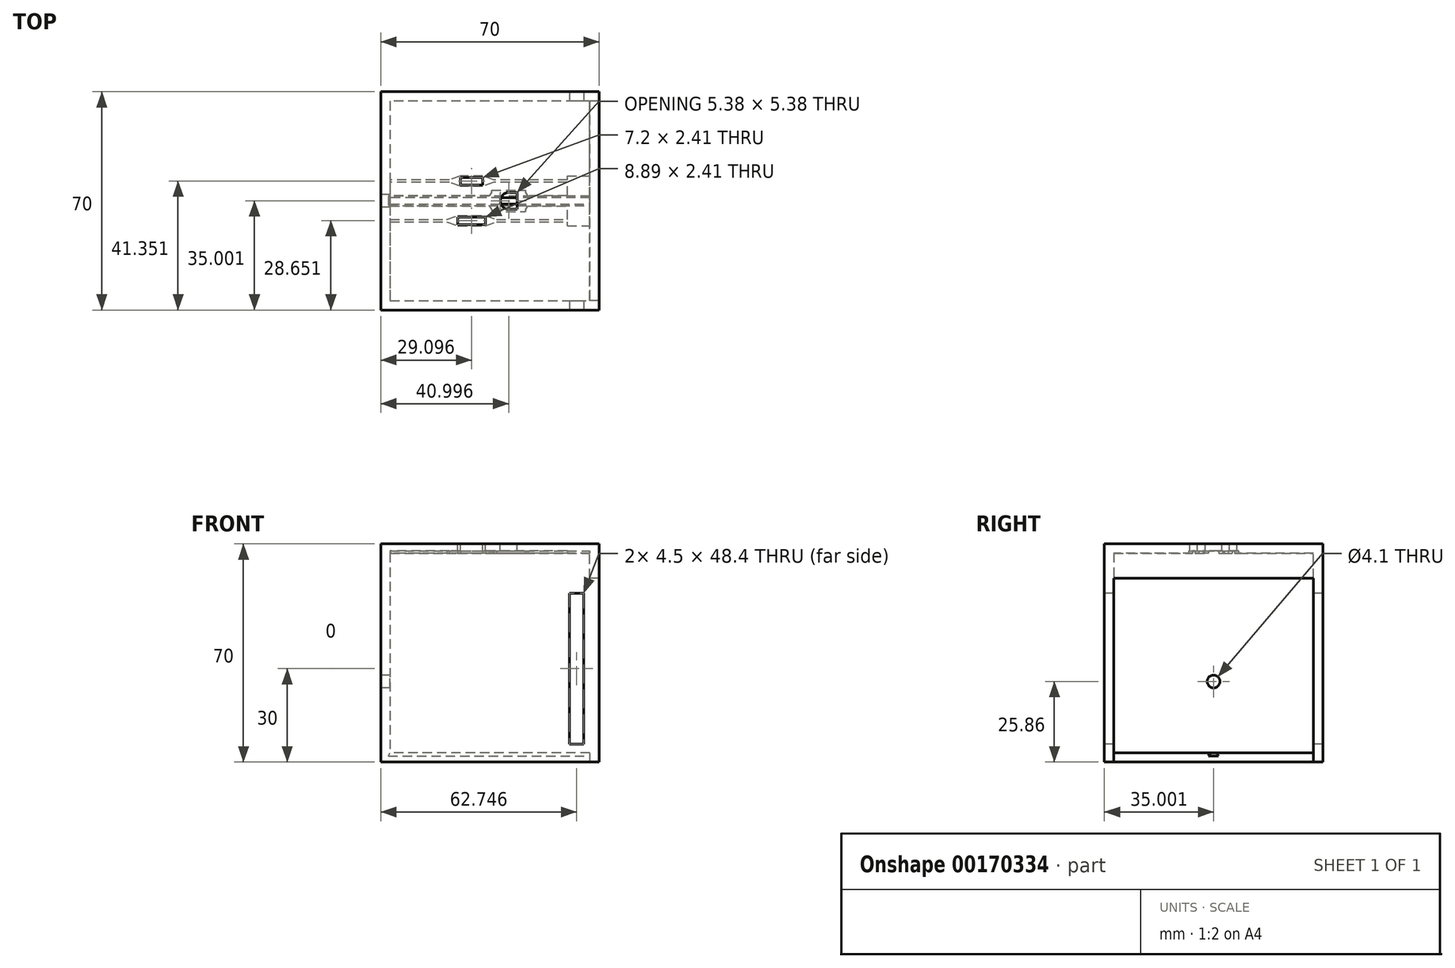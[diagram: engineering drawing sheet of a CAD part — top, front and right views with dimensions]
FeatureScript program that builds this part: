
annotation { "Feature Type Name" : "Feature", "Feature Type Description" : "" }
export const myFeature = defineFeature(function(context is Context, id is Id, definition is map)
    precondition{}
    {
        {
            var Q0;
            Q0=qCreatedBy(makeId("Top.planeOp"),FACE);
            var sketch = newSketch(context, id + "F0", { "sketchPlane" : qUnion([Q0])});
            skLineSegment(sketch, "E0", {"start": v(-33.77, 36.66) * mm, "end": v(-33.77, -33.34) * mm});
            skLineSegment(sketch, "E1", {"start": v(-33.77, -33.34) * mm, "end": v(36.23, -33.34) * mm});
            skLineSegment(sketch, "E2", {"start": v(36.23, -33.34) * mm, "end": v(36.23, 36.66) * mm});
            skLineSegment(sketch, "E3", {"start": v(36.23, 36.66) * mm, "end": v(-33.77, 36.66) * mm});
            skSolve(sketch);
        }
        {
            var Q0;
            Q0=makeQuery(id+"F0.imprint","IMPRINT",FACE,{"disambiguationData":[TD([[makeQuery(id+"F0.imprint","IMPRINT",EDGE,{"derivedFrom":sQuery(id+"F0.wireOp",EDGE,"E0")}),1.0]])]});
            extrude(context, id + "F1", {"entities" : qUnion([Q0]), "depth" : 70 * mm});
        }
        {
            var Q0;
            Q0=makeQuery(id+"F1.opExtrude","SWEPT_FACE",FACE,{"disambiguationData":[OSD([sQuery(id+"F0.wireOp",EDGE,"E2")])]});
            shell(context, id + "F2", {"entities" : qUnion([Q0]), "thickness" : 3 * mm});
        }
        {
            var Q0;
            Q0=makeQuery(id+"F1.opExtrude","CAP_FACE",FACE,{"disambiguationData":[OSD([sQuery(id+"F0.wireOp",EDGE,"E0"),sQuery(id+"F0.wireOp",EDGE,"E1"),sQuery(id+"F0.wireOp",EDGE,"E2"),sQuery(id+"F0.wireOp",EDGE,"E3")])],"isStart":false});
            var sketch = newSketch(context, id + "F3", { "sketchPlane" : qUnion([Q0])});
            skLineSegment(sketch, "E4.bottom", {"start": v(-9.12, -5.9) * mm, "end": v(-0.23, -5.9) * mm});
            skLineSegment(sketch, "E4.top", {"start": v(-9.12, -3.48) * mm, "end": v(-0.23, -3.48) * mm});
            skLineSegment(sketch, "E4.left", {"start": v(-9.12, -5.9) * mm, "end": v(-9.12, -3.48) * mm});
            skLineSegment(sketch, "E4.right", {"start": v(-0.23, -5.9) * mm, "end": v(-0.23, -3.48) * mm});
            skCircle(sketch, "E5", {"center": v(7.23, 1.66) * mm, "radius": 2.69 * mm});
            skLineSegment(sketch, "E6", {"start": v(7.23, -1.03) * mm, "end": v(9.92, -1.03) * mm});
            skLineSegment(sketch, "E7", {"start": v(9.92, -1.03) * mm, "end": v(9.92, 4.35) * mm});
            skLineSegment(sketch, "E8", {"start": v(9.92, 4.35) * mm, "end": v(7.23, 4.35) * mm});
            skLineSegment(sketch, "E9.bottom", {"start": v(-8.27, 6.8) * mm, "end": v(-1.07, 6.8) * mm});
            skLineSegment(sketch, "E9.top", {"start": v(-8.27, 9.22) * mm, "end": v(-1.07, 9.22) * mm});
            skLineSegment(sketch, "E9.left", {"start": v(-8.27, 6.8) * mm, "end": v(-8.27, 9.22) * mm});
            skLineSegment(sketch, "E9.right", {"start": v(-1.07, 6.8) * mm, "end": v(-1.07, 9.22) * mm});
            skSolve(sketch);
        }
        {
            var Q0;
            Q0=makeQuery(id+"F3.imprint","IMPRINT",FACE,{"disambiguationData":[TD([[makeQuery(id+"F3.imprint","IMPRINT",EDGE,{"derivedFrom":sQuery(id+"F3.wireOp",EDGE,"D6qbh7yJ-Ymuc-Tgfk-DwN8-qGhhH3okYrwW.bottom")}),-1.0]])]});
            var Q1;
            Q1=makeQuery(id+"F3.imprint","IMPRINT",FACE,{"disambiguationData":[TD([[makeQuery(id+"F3.imprint","IMPRINT",EDGE,{"derivedFrom":sQuery(id+"F3.wireOp",EDGE,"E4.bottom")}),1.0]])]});
            var Q2;
            {var subQ0=sQuery(id+"F3.wireOp",EDGE,"E5");var subQ1=makeQuery(id+"F3.imprint","INTERSECT",VERTEX,{"derivedFrom":[subQ0,sQuery(id+"F3.wireOp",EDGE,"E6")]});Q2=makeQuery(id+"F3.imprint","IMPRINT",FACE,{"disambiguationData":[TD([[makeQuery(id+"F3.imprint","IMPRINT",EDGE,{"disambiguationData":[TD([[subQ1,1.0]])],"derivedFrom":subQ0}),1.0]])]});}
            var Q3;
            {var subQ0=sQuery(id+"F3.wireOp",EDGE,"E6");Q3=makeQuery(id+"F3.imprint","IMPRINT",FACE,{"disambiguationData":[TD([[makeQuery(id+"F3.imprint","IMPRINT",EDGE,{"derivedFrom":subQ0}),1.0]])]});}
            var Q4;
            Q4=makeQuery(id+"F3.imprint","IMPRINT",FACE,{"disambiguationData":[TD([[makeQuery(id+"F3.imprint","IMPRINT",EDGE,{"derivedFrom":sQuery(id+"F3.wireOp",EDGE,"E9.bottom")}),1.0]])]});
            var Q5;
            {var subQ0=sQuery(id+"F3.wireOp",EDGE,"E8");Q5=makeQuery(id+"F3.imprint","IMPRINT",FACE,{"disambiguationData":[TD([[makeQuery(id+"F3.imprint","IMPRINT",EDGE,{"derivedFrom":subQ0}),1.0]])]});}
            extrude(context, id + "F4", {"entities" : qUnion([Q0, Q1, Q2, Q3, Q4, Q5]), "operationType" : NewBodyOperationType.REMOVE, "oppositeDirection" : true, "depth" : 2.54 * mm});
        }
        {
            var Q0;
            {var subQ0=sQuery(id+"F0.wireOp",EDGE,"E3");var subQ1=sQuery(id+"F0.wireOp",EDGE,"E2");var subQ2=sQuery(id+"F0.wireOp",EDGE,"E1");var subQ3=sQuery(id+"F0.wireOp",EDGE,"E0");Q0=makeQuery(id+"F2.opShell","OFFSET_FACE",FACE,{"disambiguationData":[OSD([subQ3,subQ2,subQ1,subQ0]),TDD([makeQuery(id+"F1.opExtrude","CAP_FACE",FACE,{"disambiguationData":[OSD([subQ3,subQ2,subQ1,subQ0])],"isStart":false})])]});}
            var sketch = newSketch(context, id + "F5", { "sketchPlane" : qUnion([Q0])});
            skLineSegment(sketch, "E10.bottom", {"start": v(36.23, 30.34) * mm, "end": v(33.23, 30.34) * mm});
            skLineSegment(sketch, "E10.top", {"start": v(36.23, -33.66) * mm, "end": v(33.23, -33.66) * mm});
            skLineSegment(sketch, "E10.left", {"start": v(36.23, 30.34) * mm, "end": v(36.23, -33.66) * mm});
            skLineSegment(sketch, "E10.right", {"start": v(33.23, 30.34) * mm, "end": v(33.23, -33.66) * mm});
            skSolve(sketch);
        }
        {
            var Q0;
            Q0=makeQuery(id+"F5.imprint","IMPRINT",FACE,{"disambiguationData":[TD([[makeQuery(id+"F5.imprint","IMPRINT",EDGE,{"derivedFrom":sQuery(id+"F5.wireOp",EDGE,"E10.bottom")}),-1.0]])]});
            extrude(context, id + "F6", {"entities" : qUnion([Q0]), "operationType" : NewBodyOperationType.ADD, "depth" : 8 * mm});
        }
        {
            var Q0;
            Q0=makeQuery(id+"F1.opExtrude","SWEPT_FACE",FACE,{"disambiguationData":[OSD([sQuery(id+"F0.wireOp",EDGE,"E0")])]});
            var sketch = newSketch(context, id + "F7", { "sketchPlane" : qUnion([Q0])});
            skCircle(sketch, "E11", {"center": v(-1.66, 25.86) * mm, "radius": 2.05 * mm});
            skPoint(sketch, "E11.centerSnap0", {"position": v(-1.66, 70) * mm});
            skSolve(sketch);
        }
        {
            var Q0;
            Q0=makeQuery(id+"F7.imprint","IMPRINT",FACE,{"disambiguationData":[TD([[makeQuery(id+"F7.imprint","IMPRINT",EDGE,{"derivedFrom":sQuery(id+"F7.wireOp",EDGE,"E11")}),1.0]])]});
            extrude(context, id + "F8", {"entities" : qUnion([Q0]), "operationType" : NewBodyOperationType.REMOVE, "oppositeDirection" : true, "depth" : 3.3 * mm});
        }
        {
            var Q0;
            Q0=makeQuery(id+"F1.opExtrude","SWEPT_FACE",FACE,{"disambiguationData":[OSD([sQuery(id+"F0.wireOp",EDGE,"E1")])]});
            var sketch = newSketch(context, id + "F9", { "sketchPlane" : qUnion([Q0])});
            skLineSegment(sketch, "E12.bottom", {"start": v(31.23, 54.2) * mm, "end": v(26.73, 54.2) * mm});
            skLineSegment(sketch, "E12.top", {"start": v(31.23, 5.8) * mm, "end": v(26.73, 5.8) * mm});
            skLineSegment(sketch, "E12.left", {"start": v(31.23, 54.2) * mm, "end": v(31.23, 5.8) * mm});
            skLineSegment(sketch, "E12.right", {"start": v(26.73, 54.2) * mm, "end": v(26.73, 5.8) * mm});
            skSolve(sketch);
        }
        {
            var Q0;
            Q0=makeQuery(id+"F9.imprint","IMPRINT",FACE,{"disambiguationData":[TD([[makeQuery(id+"F9.imprint","IMPRINT",EDGE,{"derivedFrom":sQuery(id+"F9.wireOp",EDGE,"E12.bottom")}),1.0]])]});
            extrude(context, id + "F10", {"entities" : qUnion([Q0]), "operationType" : NewBodyOperationType.REMOVE, "oppositeDirection" : true, "depth" : 99.57 * mm});
        }
        {
            var Q0;
            {var subQ0=sQuery(id+"F0.wireOp",EDGE,"E3");var subQ1=sQuery(id+"F0.wireOp",EDGE,"E2");var subQ2=sQuery(id+"F0.wireOp",EDGE,"E1");var subQ3=sQuery(id+"F0.wireOp",EDGE,"E0");Q0=makeQuery(id+"F2.opShell","OFFSET_FACE",FACE,{"disambiguationData":[OSD([subQ3,subQ2,subQ1,subQ0]),TDD([makeQuery(id+"F1.opExtrude","CAP_FACE",FACE,{"disambiguationData":[OSD([subQ3,subQ2,subQ1,subQ0])],"isStart":true})])]});}
            var sketch = newSketch(context, id + "F11", { "sketchPlane" : qUnion([Q0])});
            skLineSegment(sketch, "E13.bottom", {"start": v(-30.77, 0.66) * mm, "end": v(36.23, 0.66) * mm});
            skLineSegment(sketch, "E13.top", {"start": v(-30.77, 2.66) * mm, "end": v(36.23, 2.66) * mm});
            skLineSegment(sketch, "E13.left", {"start": v(-30.77, 0.66) * mm, "end": v(-30.77, 2.66) * mm});
            skLineSegment(sketch, "E13.right", {"start": v(36.23, 0.66) * mm, "end": v(36.23, 2.66) * mm});
            skSolve(sketch);
        }
        {
            var Q0;
            Q0=makeQuery(id+"F11.imprint","IMPRINT",FACE,{"disambiguationData":[TD([[makeQuery(id+"F11.imprint","IMPRINT",EDGE,{"derivedFrom":sQuery(id+"F11.wireOp",EDGE,"E13.bottom")}),1.0]])]});
            extrude(context, id + "F12", {"entities" : qUnion([Q0]), "operationType" : NewBodyOperationType.REMOVE, "oppositeDirection" : true, "depth" : 1 * mm, "hasDraft" : true, "draftAngle" : 30 * degree});
        }
        {
            var Q0;
            {var subQ0=sQuery(id+"F0.wireOp",EDGE,"E1");var subQ1=sQuery(id+"F0.wireOp",EDGE,"E0");var subQ2=sQuery(id+"F0.wireOp",EDGE,"E3");var subQ3=sQuery(id+"F0.wireOp",EDGE,"E2");Q0=makeQuery(id+"FPL7bmjeFJR5mWg_1.boolean.opBoolean","SPLIT",FACE,{"disambiguationData":[TD([makeQuery(id+"F2.opShell","OFFSET_FACE",FACE,{"disambiguationData":[OSD([subQ0])]})])],"derivedFrom":makeQuery(id+"F2.opShell","OFFSET_FACE",FACE,{"disambiguationData":[OSD([subQ1,subQ0,subQ3,subQ2]),TDD([makeQuery(id+"F1.opExtrude","CAP_FACE",FACE,{"disambiguationData":[OSD([subQ1,subQ0,subQ3,subQ2])],"isStart":false})])]})});}
            var sketch = newSketch(context, id + "F13", { "sketchPlane" : qUnion([Q0])});
            skLineSegment(sketch, "E14", {"start": v(-30.77, -3.31) * mm, "end": v(-30.77, -0.01) * mm});
            skLineSegment(sketch, "E15", {"start": v(-30.77, -0.01) * mm, "end": v(1.03, -0.01) * mm});
            skLineSegment(sketch, "E16", {"start": v(1.03, -0.01) * mm, "end": v(1.78, 1.29) * mm});
            skLineSegment(sketch, "E17", {"start": v(12.58, 1.29) * mm, "end": v(13.33, -0.01) * mm});
            skLineSegment(sketch, "E18", {"start": v(13.33, -0.01) * mm, "end": v(33.23, -0.01) * mm});
            skLineSegment(sketch, "E19", {"start": v(33.23, -0.01) * mm, "end": v(33.23, -3.31) * mm});
            skLineSegment(sketch, "E20", {"start": v(33.23, -3.31) * mm, "end": v(13.33, -3.31) * mm});
            skLineSegment(sketch, "E21", {"start": v(13.33, -3.31) * mm, "end": v(12.58, -4.61) * mm});
            skLineSegment(sketch, "E22", {"start": v(1.78, -4.61) * mm, "end": v(1.03, -3.31) * mm});
            skLineSegment(sketch, "E23", {"start": v(1.03, -3.31) * mm, "end": v(-30.77, -3.31) * mm});
            skLineSegment(sketch, "E24", {"start": v(1.78, -4.61) * mm, "end": v(1.78, -5.11) * mm});
            skLineSegment(sketch, "E25", {"start": v(1.78, -5.11) * mm, "end": v(12.58, -5.11) * mm});
            skLineSegment(sketch, "E26", {"start": v(12.58, -5.11) * mm, "end": v(12.58, -4.61) * mm});
            skLineSegment(sketch, "E27", {"start": v(1.78, 1.29) * mm, "end": v(1.78, 1.79) * mm});
            skLineSegment(sketch, "E28", {"start": v(1.78, 1.79) * mm, "end": v(12.58, 1.79) * mm});
            skLineSegment(sketch, "E29", {"start": v(12.58, 1.29) * mm, "end": v(12.58, 1.79) * mm});
            skSolve(sketch);
        }
        {
            var Q0;
            Q0 = qSketchRegion(id + "F13", true);
            extrude(context, id + "F14", {"entities" : qUnion([Q0]), "operationType" : NewBodyOperationType.REMOVE, "oppositeDirection" : true, "depth" : 0.8 * mm});
        }
        {
            var Q0;
            {var subQ8=sQuery(id+"F0.wireOp",EDGE,"E0");var subQ12=sQuery(id+"F0.wireOp",EDGE,"E1");var subQ13=makeQuery(id+"F2.opShell","OFFSET_FACE",FACE,{"disambiguationData":[OSD([subQ12])]});var subQ15=sQuery(id+"F0.wireOp",EDGE,"E3");var subQ16=sQuery(id+"F0.wireOp",EDGE,"E2");Q0=makeQuery(id+"F14.boolean.opBoolean","SPLIT",FACE,{"disambiguationData":[TD([subQ13])],"derivedFrom":makeQuery(id+"FPL7bmjeFJR5mWg_1.boolean.opBoolean","SPLIT",FACE,{"disambiguationData":[TD([subQ13])],"derivedFrom":makeQuery(id+"F2.opShell","OFFSET_FACE",FACE,{"disambiguationData":[OSD([subQ8,subQ12,subQ16,subQ15]),TDD([makeQuery(id+"F1.opExtrude","CAP_FACE",FACE,{"disambiguationData":[OSD([subQ8,subQ12,subQ16,subQ15])],"isStart":false})])]})})});}
            var sketch = newSketch(context, id + "F15", { "sketchPlane" : qUnion([Q0])});
            skLineSegment(sketch, "E30.bottom", {"start": v(-30.77, 4.25) * mm, "end": v(-30.77, 5.05) * mm});
            skLineSegment(sketch, "E30.top", {"start": v(33.23, 4.25) * mm, "end": v(33.23, 5.05) * mm});
            skLineSegment(sketch, "E31", {"start": v(-12.63, 4.25) * mm, "end": v(-9.12, 3.02) * mm});
            skLineSegment(sketch, "E32", {"start": v(-9.12, 3.02) * mm, "end": v(-0.23, 3.02) * mm});
            skLineSegment(sketch, "E33", {"start": v(-0.23, 3.02) * mm, "end": v(3.28, 4.25) * mm});
            skLineSegment(sketch, "E34", {"start": v(-12.63, 5.05) * mm, "end": v(-9.12, 6.27) * mm});
            skLineSegment(sketch, "E35", {"start": v(-9.12, 6.27) * mm, "end": v(-0.23, 6.27) * mm});
            skLineSegment(sketch, "E36", {"start": v(-0.23, 6.27) * mm, "end": v(3.28, 5.05) * mm});
            skLineSegment(sketch, "E37", {"start": v(-30.77, 4.25) * mm, "end": v(-12.63, 4.25) * mm});
            skLineSegment(sketch, "E38", {"start": v(3.28, 4.25) * mm, "end": v(33.23, 4.25) * mm});
            skLineSegment(sketch, "E39", {"start": v(-30.77, 5.05) * mm, "end": v(-12.63, 5.05) * mm});
            skLineSegment(sketch, "E40", {"start": v(3.28, 5.05) * mm, "end": v(33.23, 5.05) * mm});
            skSolve(sketch);
        }
        {
            var Q0;
            Q0=makeQuery(id+"F15.imprint","IMPRINT",FACE,{"disambiguationData":[TD([[makeQuery(id+"F15.imprint","IMPRINT",EDGE,{"derivedFrom":sQuery(id+"F15.wireOp",EDGE,"E30.bottom")}),-1.0]])]});
            extrude(context, id + "F16", {"entities" : qUnion([Q0]), "operationType" : NewBodyOperationType.REMOVE, "oppositeDirection" : true, "depth" : 0.8 * mm});
        }
        {
            var Q0;
            {var subQ2=sQuery(id+"F0.wireOp",EDGE,"E0");var subQ6=sQuery(id+"F0.wireOp",EDGE,"E1");var subQ7=makeQuery(id+"F2.opShell","OFFSET_FACE",FACE,{"disambiguationData":[OSD([subQ6])]});var subQ9=sQuery(id+"F0.wireOp",EDGE,"E3");var subQ10=sQuery(id+"F0.wireOp",EDGE,"E2");Q0=makeQuery(id+"F16.boolean.opBoolean","SPLIT",FACE,{"disambiguationData":[TD([subQ7])],"derivedFrom":makeQuery(id+"F14.boolean.opBoolean","SPLIT",FACE,{"disambiguationData":[TD([subQ7])],"derivedFrom":makeQuery(id+"FPL7bmjeFJR5mWg_1.boolean.opBoolean","SPLIT",FACE,{"disambiguationData":[TD([subQ7])],"derivedFrom":makeQuery(id+"F2.opShell","OFFSET_FACE",FACE,{"disambiguationData":[OSD([subQ2,subQ6,subQ10,subQ9]),TDD([makeQuery(id+"F1.opExtrude","CAP_FACE",FACE,{"disambiguationData":[OSD([subQ2,subQ6,subQ10,subQ9])],"isStart":false})])]})})})});}
            var sketch = newSketch(context, id + "F17", { "sketchPlane" : qUnion([Q0])});
            skLineSegment(sketch, "E41.bottom", {"start": v(26.03, 6.34) * mm, "end": v(33.23, 6.34) * mm});
            skLineSegment(sketch, "E41.top", {"start": v(26.03, -9.66) * mm, "end": v(33.23, -9.66) * mm});
            skLineSegment(sketch, "E41.left", {"start": v(26.03, 6.34) * mm, "end": v(26.03, -9.66) * mm});
            skLineSegment(sketch, "E41.right", {"start": v(33.23, 6.34) * mm, "end": v(33.23, -9.66) * mm});
            skSolve(sketch);
        }
        {
            var Q0;
            {var subQ0=sQuery(id+"F17.wireOp",EDGE,"E41.bottom");Q0=makeQuery(id+"F17.imprint","IMPRINT",FACE,{"disambiguationData":[TD([[makeQuery(id+"F17.imprint","IMPRINT",EDGE,{"derivedFrom":subQ0}),-1.0]])]});}
            var Q1;
            {var subQ0=sQuery(id+"F17.wireOp",EDGE,"E41.top");Q1=makeQuery(id+"F17.imprint","IMPRINT",FACE,{"disambiguationData":[TD([[makeQuery(id+"F17.imprint","IMPRINT",EDGE,{"derivedFrom":subQ0}),1.0]])]});}
            extrude(context, id + "F18", {"entities" : qUnion([Q0, Q1]), "operationType" : NewBodyOperationType.REMOVE, "oppositeDirection" : true, "depth" : 0.8 * mm});
        }
        {
            var Q0;
            {var subQ0=sQuery(id+"F0.wireOp",EDGE,"E0");var subQ1=sQuery(id+"F0.wireOp",EDGE,"E3");var subQ2=sQuery(id+"F0.wireOp",EDGE,"E2");var subQ3=sQuery(id+"F0.wireOp",EDGE,"E1");Q0=makeQuery(id+"F14.boolean.opBoolean","SPLIT",FACE,{"disambiguationData":[TD([makeQuery(id+"F2.opShell","OFFSET_FACE",FACE,{"disambiguationData":[OSD([subQ1])]})])],"derivedFrom":makeQuery(id+"F2.opShell","OFFSET_FACE",FACE,{"disambiguationData":[OSD([subQ0,subQ3,subQ2,subQ1]),TDD([makeQuery(id+"F1.opExtrude","CAP_FACE",FACE,{"disambiguationData":[OSD([subQ0,subQ3,subQ2,subQ1])],"isStart":false})])]})});}
            var sketch = newSketch(context, id + "F19", { "sketchPlane" : qUnion([Q0])});
            skLineSegment(sketch, "E42.bottom", {"start": v(26.03, -7.61) * mm, "end": v(26.03, -8.41) * mm});
            skLineSegment(sketch, "E42.top", {"start": v(-30.77, -7.61) * mm, "end": v(-30.77, -8.41) * mm});
            skLineSegment(sketch, "E43", {"start": v(2.44, -7.61) * mm, "end": v(-1.07, -6.38) * mm});
            skLineSegment(sketch, "E44", {"start": v(-1.07, -6.38) * mm, "end": v(-8.27, -6.38) * mm});
            skLineSegment(sketch, "E45", {"start": v(-8.27, -6.38) * mm, "end": v(-11.79, -7.61) * mm});
            skLineSegment(sketch, "E46", {"start": v(2.44, -8.41) * mm, "end": v(-1.07, -9.64) * mm});
            skLineSegment(sketch, "E47", {"start": v(-1.07, -9.64) * mm, "end": v(-8.27, -9.64) * mm});
            skLineSegment(sketch, "E48", {"start": v(-8.27, -9.64) * mm, "end": v(-11.79, -8.41) * mm});
            skLineSegment(sketch, "E49", {"start": v(26.03, -7.61) * mm, "end": v(2.44, -7.61) * mm});
            skLineSegment(sketch, "E50", {"start": v(-11.79, -7.61) * mm, "end": v(-30.77, -7.61) * mm});
            skLineSegment(sketch, "E51", {"start": v(26.03, -8.41) * mm, "end": v(2.44, -8.41) * mm});
            skLineSegment(sketch, "E52", {"start": v(-11.79, -8.41) * mm, "end": v(-30.77, -8.41) * mm});
            skSolve(sketch);
        }
        {
            var Q0;
            Q0=makeQuery(id+"F19.imprint","IMPRINT",FACE,{"disambiguationData":[TD([[makeQuery(id+"F19.imprint","IMPRINT",EDGE,{"derivedFrom":sQuery(id+"F19.wireOp",EDGE,"E42.bottom")}),-1.0]])]});
            extrude(context, id + "F20", {"entities" : qUnion([Q0]), "operationType" : NewBodyOperationType.REMOVE, "oppositeDirection" : true, "depth" : 0.8 * mm});
        }
        {
            var Q0;
            Q0=makeQuery(id+"F1.opExtrude","CAP_FACE",FACE,{"disambiguationData":[OSD([sQuery(id+"F0.wireOp",EDGE,"E0"),sQuery(id+"F0.wireOp",EDGE,"E1"),sQuery(id+"F0.wireOp",EDGE,"E2"),sQuery(id+"F0.wireOp",EDGE,"E3")])],"isStart":true});
            var sketch = newSketch(context, id + "F21", { "sketchPlane" : qUnion([Q0])});
            skLineSegment(sketch, "E53.bottom", {"start": v(36.23, 30.34) * mm, "end": v(33.23, 30.34) * mm});
            skLineSegment(sketch, "E53.top", {"start": v(36.23, -33.66) * mm, "end": v(33.23, -33.66) * mm});
            skLineSegment(sketch, "E53.left", {"start": v(36.23, 30.34) * mm, "end": v(36.23, -33.66) * mm});
            skLineSegment(sketch, "E53.right", {"start": v(33.23, 30.34) * mm, "end": v(33.23, -33.66) * mm});
            skSolve(sketch);
        }
        {
            var Q0;
            Q0=makeQuery(id+"F21.imprint","IMPRINT",FACE,{"disambiguationData":[TD([[makeQuery(id+"F21.imprint","IMPRINT",EDGE,{"derivedFrom":sQuery(id+"F21.wireOp",EDGE,"E53.bottom")}),1.0]])]});
            extrude(context, id + "F22", {"entities" : qUnion([Q0]), "operationType" : NewBodyOperationType.REMOVE, "oppositeDirection" : true, "depth" : 4.6 * mm});
        }
    });
